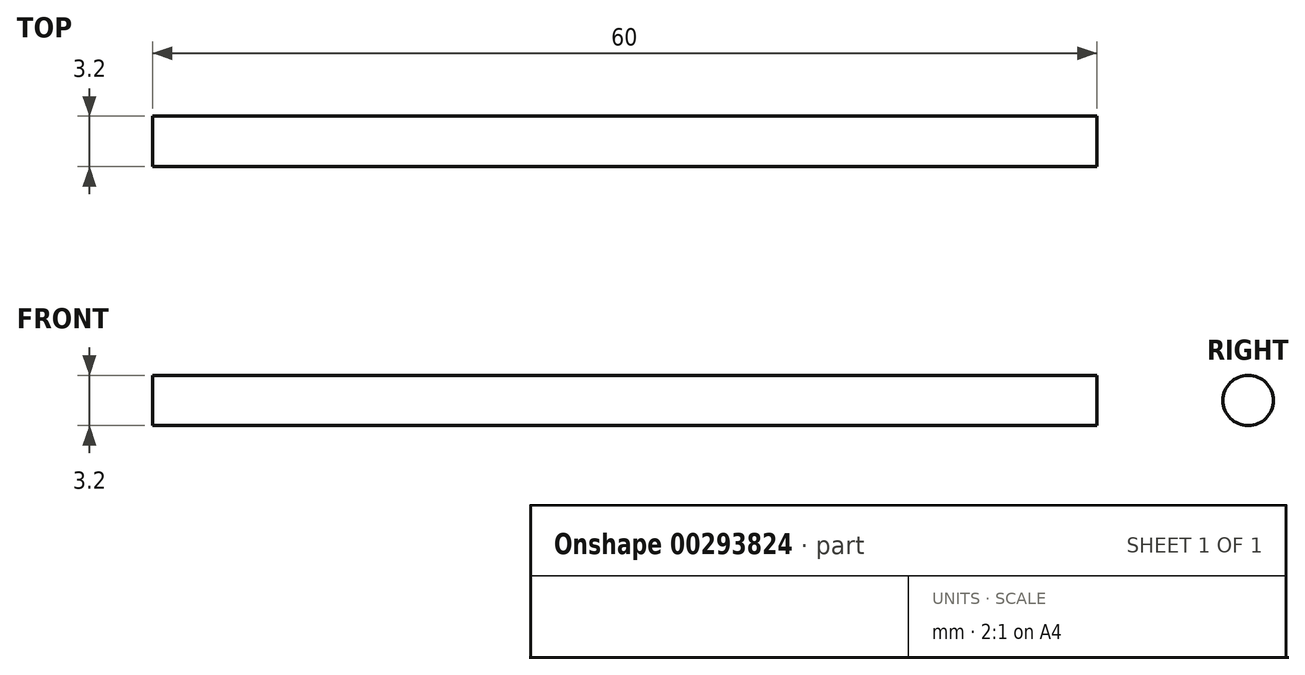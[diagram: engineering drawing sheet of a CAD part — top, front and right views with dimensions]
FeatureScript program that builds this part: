
annotation { "Feature Type Name" : "Feature", "Feature Type Description" : "" }
export const myFeature = defineFeature(function(context is Context, id is Id, definition is map)
    precondition{}
    {
        {
            var Q0;
            Q0=qCreatedBy(makeId("Right.planeOp"),FACE);
            var sketch = newSketch(context, id + "F0", { "sketchPlane" : qUnion([Q0])});
            skCircle(sketch, "E0", {"center": v(0, 0) * mm, "radius": 1.6 * mm});
            skSolve(sketch);
        }
        {
            var Q0;
            Q0=makeQuery(id+"F0.imprint","IMPRINT",FACE,{"disambiguationData":[TD([[makeQuery(id+"F0.imprint","IMPRINT",EDGE,{"derivedFrom":sQuery(id+"F0.wireOp",EDGE,"E0")}),1.0]])]});
            extrude(context, id + "F1", {"entities" : qUnion([Q0]), "endBound" : BoundingType.SYMMETRIC, "depth" : 60 * mm});
        }
    });
